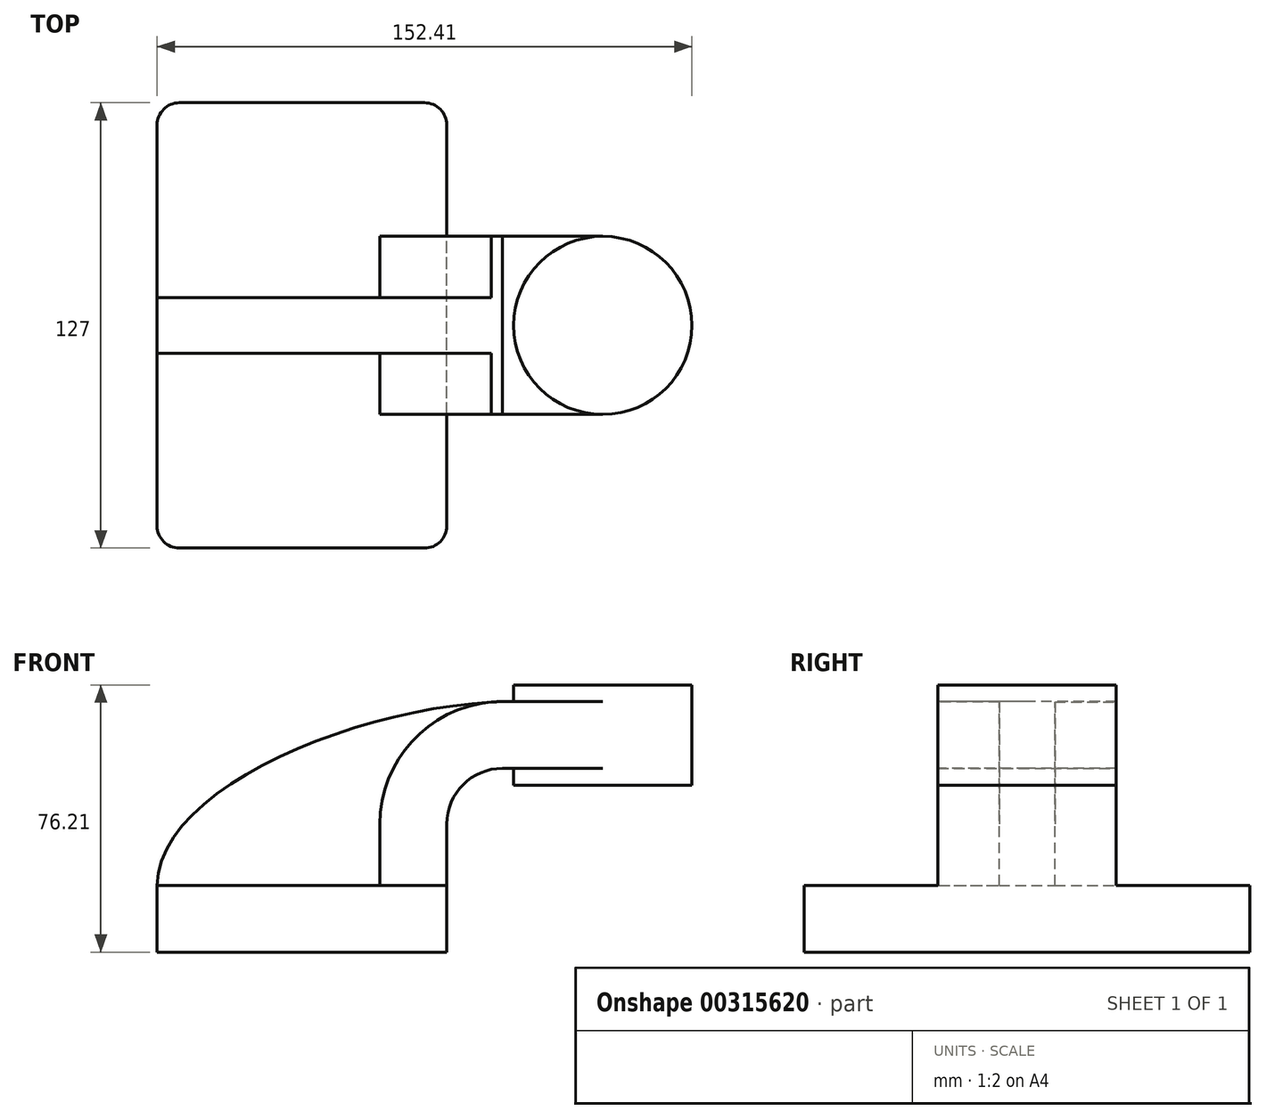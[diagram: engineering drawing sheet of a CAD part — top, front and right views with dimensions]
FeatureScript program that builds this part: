
annotation { "Feature Type Name" : "Feature", "Feature Type Description" : "" }
export const myFeature = defineFeature(function(context is Context, id is Id, definition is map)
    precondition{}
    {
        {
            var Q0;
            Q0=qCreatedBy(makeId("Front.planeOp"),FACE);
            var sketch = newSketch(context, id + "F0", { "sketchPlane" : qUnion([Q0])});
            skLineSegment(sketch, "E0.bottom", {"start": v(-41.28, 9.52) * mm, "end": v(41.28, 9.53) * mm});
            skLineSegment(sketch, "E0.top", {"start": v(-41.28, -9.53) * mm, "end": v(41.28, -9.53) * mm});
            skLineSegment(sketch, "E0.left", {"start": v(-41.28, 9.52) * mm, "end": v(-41.28, -9.53) * mm});
            skLineSegment(sketch, "E0.right", {"start": v(41.28, 9.53) * mm, "end": v(41.28, -9.52) * mm});
            skPoint(sketch, "E0.middle", {"position": v(0, 0) * mm});
            skLineSegment(sketch, "E1", {"start": v(41.27, 9.53) * mm, "end": v(41.27, 27) * mm});
            skArc(sketch, "E2", {"start": v(41.27, 27) * mm, "mid": v(45.92, 38.23) * mm, "end": v(57.15, 42.88) * mm});
            skLineSegment(sketch, "E3.bottom", {"start": v(111.12, 38.1) * mm, "end": v(60.32, 38.1) * mm});
            skLineSegment(sketch, "E3.top", {"start": v(111.13, 66.68) * mm, "end": v(60.32, 66.68) * mm});
            skLineSegment(sketch, "E3.left", {"start": v(111.13, 38.1) * mm, "end": v(111.13, 66.68) * mm});
            skLineSegment(sketch, "E3.right", {"start": v(60.32, 38.1) * mm, "end": v(60.32, 66.68) * mm});
            skPoint(sketch, "E3.middle", {"position": v(85.73, 52.39) * mm});
            skLineSegment(sketch, "E4", {"start": v(57.15, 42.88) * mm, "end": v(85.73, 42.88) * mm});
            skLineSegment(sketch, "E5.0", {"start": v(57.15, 61.93) * mm, "end": v(85.73, 61.93) * mm});
            skArc(sketch, "E5.1", {"start": v(22.22, 27) * mm, "mid": v(32.45, 51.7) * mm, "end": v(57.15, 61.93) * mm});
            skLineSegment(sketch, "E5.2", {"start": v(22.22, 9.53) * mm, "end": v(22.22, 27) * mm});
            skLineSegment(sketch, "E6", {"start": v(85.72, 38.1) * mm, "end": v(85.72, 66.68) * mm});
            skFitSpline(sketch, "E7", {"points": [v(-41.28, 9.53) * mm, v(57.15, 61.93) * mm], "startDerivative": vector(0.94, 83.73) * mm, "endDerivative": vector(123.28, 4.06) * mm});
            skSolve(sketch);
        }
        {
            var Q0;
            Q0=makeQuery(id+"F0.imprint","IMPRINT",FACE,{"disambiguationData":[TD([[makeQuery(id+"F0.imprint","IMPRINT",EDGE,{"derivedFrom":sQuery(id+"F0.wireOp",EDGE,"E0.top")}),1.0]])]});
            extrude(context, id + "F1", {"entities" : qUnion([Q0]), "endBound" : BoundingType.SYMMETRIC, "depth" : 127 * mm});
        }
        {
            var Q0;
            {var subQ5=sQuery(id+"F0.wireOp",EDGE,"E1");Q0=makeQuery(id+"F0.imprint","IMPRINT",FACE,{"disambiguationData":[TD([[makeQuery(id+"F0.imprint","IMPRINT",EDGE,{"derivedFrom":subQ5}),1.0]])]});}
            var Q1;
            {var subQ0=sQuery(id+"F0.wireOp",EDGE,"E4");var subQ1=sQuery(id+"F0.wireOp",EDGE,"E3.right");var subQ2=makeQuery(id+"F0.imprint","INTERSECT",VERTEX,{"derivedFrom":[subQ1,subQ0]});Q1=makeQuery(id+"F0.imprint","IMPRINT",FACE,{"disambiguationData":[TD([[makeQuery(id+"F0.imprint","IMPRINT",EDGE,{"disambiguationData":[TD([[subQ2,-1.0]])],"derivedFrom":subQ1}),-1.0]])]});}
            extrude(context, id + "F2", {"entities" : qUnion([Q0, Q1]), "operationType" : NewBodyOperationType.ADD, "endBound" : BoundingType.SYMMETRIC, "depth" : 50.8 * mm});
        }
        {
            var Q0;
            {var subQ3=sQuery(id+"F0.wireOp",EDGE,"E5.2");Q0=makeQuery(id+"F0.imprint","IMPRINT",FACE,{"disambiguationData":[TD([[makeQuery(id+"F0.imprint","IMPRINT",EDGE,{"derivedFrom":subQ3}),1.0]])]});}
            extrude(context, id + "F3", {"entities" : qUnion([Q0]), "operationType" : NewBodyOperationType.ADD, "endBound" : BoundingType.SYMMETRIC, "depth" : 15.88 * mm});
        }
        {
            var Q0;
            {var subQ0=sQuery(id+"F0.wireOp",EDGE,"E3.left");Q0=makeQuery(id+"F0.imprint","IMPRINT",FACE,{"disambiguationData":[TD([[makeQuery(id+"F0.imprint","IMPRINT",EDGE,{"derivedFrom":subQ0}),1.0]])]});}
            var Q1;
            Q1=sQuery(id+"F0.wireOp",EDGE,"E6");
            revolve(context, id + "F4", {"operationType" : NewBodyOperationType.ADD, "entities" : qUnion([Q0]), "axis" : qUnion([Q1]), "revolveType" : RevolveType.FULL});
        }
        {
            var Q0;
            Q0=makeQuery(id+"F1.opExtrude","CAP_EDGE",EDGE,{"disambiguationData":[OSD([sQuery(id+"F0.wireOp",EDGE,"E0.left")])],"isStart":false});
            var Q1;
            Q1=makeQuery(id+"F1.opExtrude","CAP_EDGE",EDGE,{"disambiguationData":[OSD([sQuery(id+"F0.wireOp",EDGE,"E0.right")])],"isStart":false});
            var Q2;
            Q2=makeQuery(id+"F1.opExtrude","CAP_EDGE",EDGE,{"disambiguationData":[OSD([sQuery(id+"F0.wireOp",EDGE,"E0.right")])],"isStart":true});
            var Q3;
            Q3=makeQuery(id+"F1.opExtrude","CAP_EDGE",EDGE,{"disambiguationData":[OSD([sQuery(id+"F0.wireOp",EDGE,"E0.left")])],"isStart":true});
            fillet(context, id + "F5", {"entities" : qUnion([Q0, Q1, Q2, Q3]), "radius" : 6.35 * mm, "tangentPropagation" : true, "allowEdgeOverflow" : false});
        }
    });
